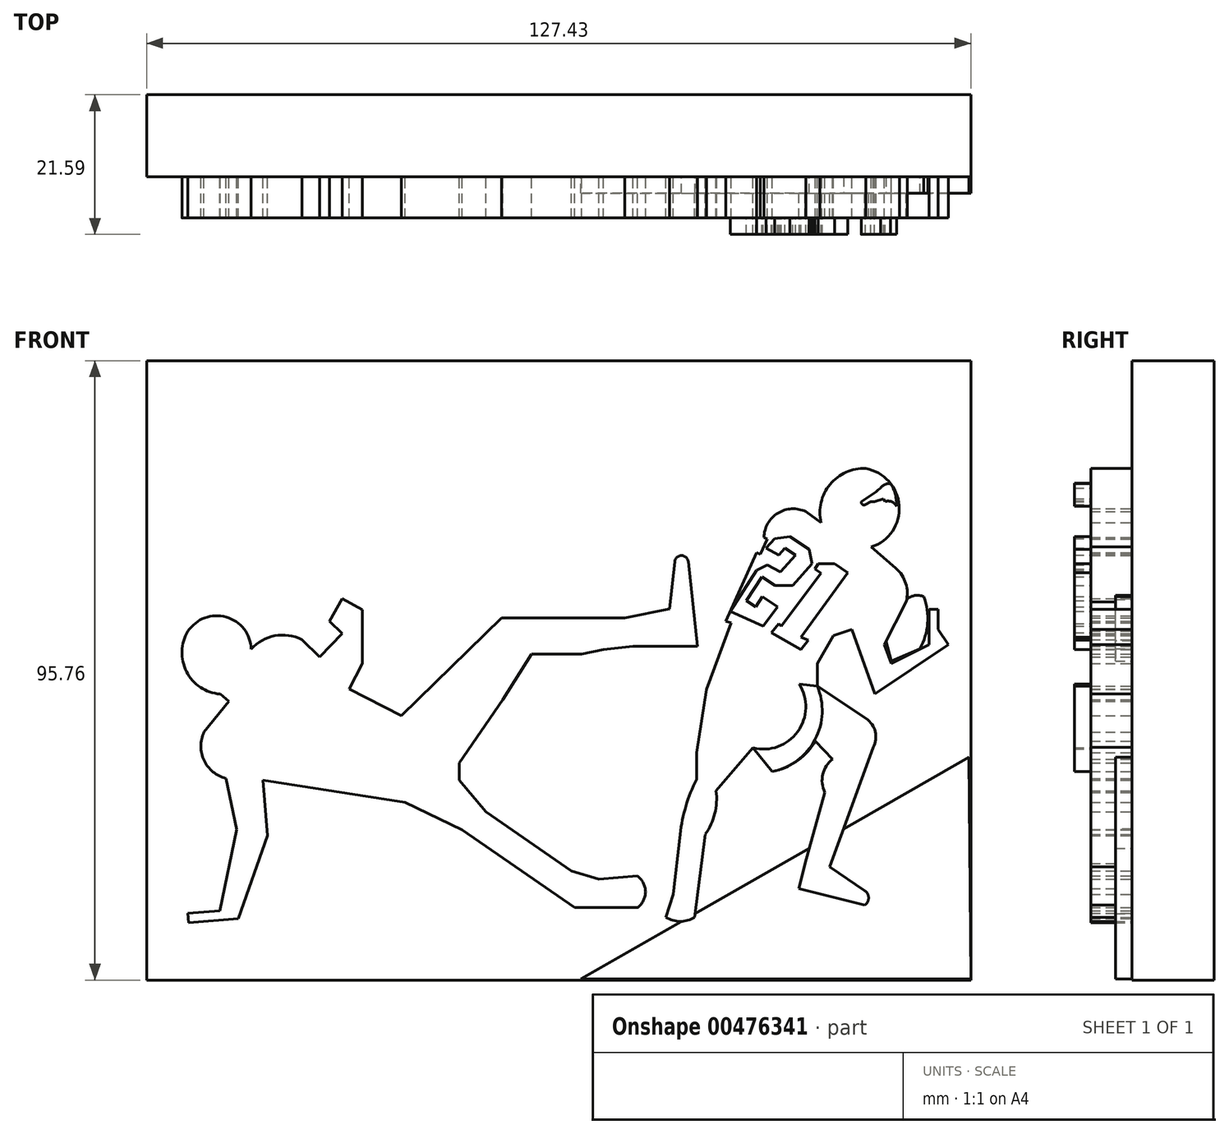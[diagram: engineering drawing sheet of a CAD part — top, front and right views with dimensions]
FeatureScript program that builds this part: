
annotation { "Feature Type Name" : "Feature", "Feature Type Description" : "" }
export const myFeature = defineFeature(function(context is Context, id is Id, definition is map)
    precondition{}
    {
        {
            var Q0;
            Q0=qCreatedBy(makeId("Front.planeOp"),FACE);
            var sketch = newSketch(context, id + "F0", { "sketchPlane" : qUnion([Q0])});
            skLineSegment(sketch, "E0.bottom", {"start": v(-88.04, 45.36) * mm, "end": v(39.4, 45.36) * mm});
            skLineSegment(sketch, "E0.top", {"start": v(-88.04, -50.4) * mm, "end": v(39.4, -50.4) * mm});
            skLineSegment(sketch, "E0.left", {"start": v(-88.04, 45.36) * mm, "end": v(-88.04, -50.4) * mm});
            skLineSegment(sketch, "E0.right", {"start": v(39.4, 45.36) * mm, "end": v(39.4, -50.4) * mm});
            skSolve(sketch);
        }
        {
            var Q0;
            Q0 = qSketchRegion(id + "F0", true);
            extrude(context, id + "F1", {"entities" : qUnion([Q0]), "depth" : 12.7 * mm});
        }
        {
            var Q0;
            Q0=makeQuery(id+"F1.opExtrude","CAP_FACE",FACE,{"disambiguationData":[OSD([sQuery(id+"F0.wireOp",EDGE,"E0.bottom"),sQuery(id+"F0.wireOp",EDGE,"E0.top"),sQuery(id+"F0.wireOp",EDGE,"E0.left"),sQuery(id+"F0.wireOp",EDGE,"E0.right")])],"isStart":false});
            var sketch = newSketch(context, id + "F2", { "sketchPlane" : qUnion([Q0])});
            skLineSegment(sketch, "E1", {"start": v(-70.07, -19.5) * mm, "end": v(-69.38, -28.1) * mm});
            skLineSegment(sketch, "E2", {"start": v(-69.38, -28.1) * mm, "end": v(-73.87, -40.93) * mm});
            skLineSegment(sketch, "E3", {"start": v(-73.87, -40.93) * mm, "end": v(-81.59, -41.55) * mm});
            skLineSegment(sketch, "E4", {"start": v(-81.59, -41.55) * mm, "end": v(-81.7, -40.06) * mm});
            skLineSegment(sketch, "E5", {"start": v(-81.7, -40.06) * mm, "end": v(-76.75, -39.66) * mm});
            skLineSegment(sketch, "E6", {"start": v(-76.75, -39.66) * mm, "end": v(-74.13, -27.12) * mm});
            skLineSegment(sketch, "E7", {"start": v(-74.13, -27.12) * mm, "end": v(-75.79, -19.23) * mm});
            skArc(sketch, "E8", {"start": v(-79.18, -12.07) * mm, "mid": v(-79.17, -16.45) * mm, "end": v(-75.79, -19.23) * mm});
            skLineSegment(sketch, "E9", {"start": v(-79.18, -12.07) * mm, "end": v(-75.33, -7.3) * mm});
            skLineSegment(sketch, "E10", {"start": v(-75.33, -7.3) * mm, "end": v(-76.7, -6.19) * mm});
            skArc(sketch, "E11", {"start": v(-81.65, 3.53) * mm, "mid": v(-81.89, -2.7) * mm, "end": v(-76.7, -6.19) * mm});
            skArc(sketch, "E12", {"start": v(-71.88, 0.74) * mm, "mid": v(-75.74, 5.72) * mm, "end": v(-81.65, 3.53) * mm});
            skArc(sketch, "E13", {"start": v(-64.06, 2.2) * mm, "mid": v(-68.22, 2.83) * mm, "end": v(-71.88, 0.74) * mm});
            skLineSegment(sketch, "E14", {"start": v(-64.06, 2.2) * mm, "end": v(-61.3, -0.45) * mm});
            skLineSegment(sketch, "E15", {"start": v(-61.3, -0.45) * mm, "end": v(-57.81, 3.16) * mm});
            skLineSegment(sketch, "E16", {"start": v(-57.81, 3.16) * mm, "end": v(-59.8, 5.08) * mm});
            skLineSegment(sketch, "E17", {"start": v(-59.8, 5.08) * mm, "end": v(-57.81, 8.58) * mm});
            skLineSegment(sketch, "E18", {"start": v(-57.81, 8.58) * mm, "end": v(-54.72, 6.83) * mm});
            skLineSegment(sketch, "E19", {"start": v(-54.72, 6.83) * mm, "end": v(-54.72, 3.16) * mm});
            skLineSegment(sketch, "E20", {"start": v(-54.72, 3.16) * mm, "end": v(-54.72, -1.48) * mm});
            skLineSegment(sketch, "E21", {"start": v(-54.72, -1.48) * mm, "end": v(-56.72, -5.4) * mm});
            skLineSegment(sketch, "E22", {"start": v(-56.72, -5.4) * mm, "end": v(-48.66, -9.52) * mm});
            skLineSegment(sketch, "E23", {"start": v(-48.66, -9.52) * mm, "end": v(-33.17, 5.59) * mm});
            skLineSegment(sketch, "E24", {"start": v(-33.17, 5.59) * mm, "end": v(-14.09, 5.59) * mm});
            skLineSegment(sketch, "E25", {"start": v(-14.09, 5.59) * mm, "end": v(-7.17, 6.98) * mm});
            skLineSegment(sketch, "E26", {"start": v(-7.17, 6.98) * mm, "end": v(-6.39, 14.29) * mm});
            skArc(sketch, "E27", {"start": v(-4.3, 14.29) * mm, "mid": v(-5.35, 15.22) * mm, "end": v(-6.39, 14.29) * mm});
            skLineSegment(sketch, "E28", {"start": v(-4.3, 14.29) * mm, "end": v(-2.9, 1.2) * mm});
            skLineSegment(sketch, "E29", {"start": v(-2.9, 1.2) * mm, "end": v(-12.85, 1.2) * mm});
            skLineSegment(sketch, "E30", {"start": v(-12.85, 1.2) * mm, "end": v(-17.44, 0.72) * mm});
            skLineSegment(sketch, "E31", {"start": v(-17.44, 0.72) * mm, "end": v(-20.76, 0) * mm});
            skLineSegment(sketch, "E32", {"start": v(-28.52, 0) * mm, "end": v(-20.76, 0) * mm});
            skLineSegment(sketch, "E33", {"start": v(-28.52, 0) * mm, "end": v(-32.95, -7.05) * mm});
            skLineSegment(sketch, "E34", {"start": v(-32.95, -7.05) * mm, "end": v(-39.73, -16.83) * mm});
            skLineSegment(sketch, "E35", {"start": v(-39.73, -16.83) * mm, "end": v(-39.73, -19.5) * mm});
            skLineSegment(sketch, "E36", {"start": v(-39.73, -19.5) * mm, "end": v(-35.57, -24.39) * mm});
            skLineSegment(sketch, "E37", {"start": v(-35.57, -24.39) * mm, "end": v(-22.34, -33.54) * mm});
            skLineSegment(sketch, "E38", {"start": v(-22.34, -33.54) * mm, "end": v(-18.15, -34.8) * mm});
            skLineSegment(sketch, "E39", {"start": v(-18.15, -34.8) * mm, "end": v(-12.17, -34.33) * mm});
            skArc(sketch, "E40", {"start": v(-12.17, -39.2) * mm, "mid": v(-10.9, -36.76) * mm, "end": v(-12.17, -34.33) * mm});
            skLineSegment(sketch, "E41", {"start": v(-12.17, -39.2) * mm, "end": v(-21.9, -39.2) * mm});
            skLineSegment(sketch, "E42", {"start": v(-21.9, -39.2) * mm, "end": v(-27.7, -35.18) * mm});
            skLineSegment(sketch, "E43", {"start": v(-27.7, -35.18) * mm, "end": v(-39.3, -27.16) * mm});
            skLineSegment(sketch, "E44", {"start": v(-39.3, -27.16) * mm, "end": v(-48.12, -22.92) * mm});
            skLineSegment(sketch, "E45", {"start": v(-48.12, -22.92) * mm, "end": v(-70.07, -19.5) * mm});
            skSolve(sketch);
        }
        {
            var Q0;
            Q0=makeQuery(id+"F2.imprint","IMPRINT",FACE,{"disambiguationData":[TD([[makeQuery(id+"F2.imprint","IMPRINT",EDGE,{"derivedFrom":sQuery(id+"F2.wireOp",EDGE,"E1")}),1.0]])]});
            var sketch = newSketch(context, id + "F3", { "sketchPlane" : qUnion([Q0])});
            skLineSegment(sketch, "E46", {"start": v(39.1, -15.97) * mm, "end": v(-20.94, -50.24) * mm});
            skLineSegment(sketch, "E47", {"start": v(39.1, -15.97) * mm, "end": v(39.39, -50.24) * mm});
            skLineSegment(sketch, "E48", {"start": v(-20.94, -50.24) * mm, "end": v(39.39, -50.24) * mm});
            skArc(sketch, "E49", {"start": v(32.1, 8.86) * mm, "mid": v(30.47, 9) * mm, "end": v(29.12, 8.06) * mm});
            skArc(sketch, "E50", {"start": v(31.51, 0.8) * mm, "mid": v(32.7, 4.77) * mm, "end": v(32.1, 8.86) * mm});
            skLineSegment(sketch, "E51", {"start": v(31.51, 0.8) * mm, "end": v(27.1, -1.08) * mm});
            skLineSegment(sketch, "E52", {"start": v(27.1, -1.08) * mm, "end": v(26.27, 2.07) * mm});
            skLineSegment(sketch, "E53", {"start": v(26.27, 2.07) * mm, "end": v(29.12, 8.06) * mm});
            skSolve(sketch);
        }
        {
            var Q0;
            Q0 = qSketchRegion(id + "F3", true);
            extrude(context, id + "F4", {"entities" : qUnion([Q0]), "depth" : 2.54 * mm});
        }
        {
            var Q0;
            Q0 = qSketchRegion(id + "F2", true);
            extrude(context, id + "F5", {"entities" : qUnion([Q0]), "depth" : 6.35 * mm});
        }
        {
            var Q0;
            Q0=makeQuery(id+"F2.imprint","IMPRINT",FACE,{"disambiguationData":[TD([[makeQuery(id+"F2.imprint","IMPRINT",EDGE,{"derivedFrom":sQuery(id+"F2.wireOp",EDGE,"E1")}),1.0]])]});
            var sketch = newSketch(context, id + "F6", { "sketchPlane" : qUnion([Q0])});
            skArc(sketch, "E54", {"start": v(-7.75, -40.7) * mm, "mid": v(-5.52, -41.33) * mm, "end": v(-3.3, -40.68) * mm});
            skLineSegment(sketch, "E55", {"start": v(-3.3, -40.68) * mm, "end": v(-1.67, -27.85) * mm});
            skLineSegment(sketch, "E56", {"start": v(-7.75, -40.7) * mm, "end": v(-6.61, -37.14) * mm});
            skLineSegment(sketch, "E57", {"start": v(-6.61, -37.14) * mm, "end": v(-5.55, -27.85) * mm});
            skArc(sketch, "E58", {"start": v(-3.03, -19.36) * mm, "mid": v(-4.66, -23.5) * mm, "end": v(-5.55, -27.85) * mm});
            skArc(sketch, "E59", {"start": v(-1.67, -27.85) * mm, "mid": v(-0.2, -24.67) * mm, "end": v(0, -21.17) * mm});
            skLineSegment(sketch, "E60", {"start": v(-3.03, -19.36) * mm, "end": v(-3.03, -15.26) * mm});
            skLineSegment(sketch, "E61", {"start": v(-3.03, -15.26) * mm, "end": v(-1.45, -5.45) * mm});
            skLineSegment(sketch, "E62", {"start": v(-1.45, -5.45) * mm, "end": v(2.32, 4.8) * mm});
            skLineSegment(sketch, "E63", {"start": v(2.32, 4.8) * mm, "end": v(1.52, 5.09) * mm});
            skLineSegment(sketch, "E64", {"start": v(1.52, 5.09) * mm, "end": v(6.25, 15.7) * mm});
            skLineSegment(sketch, "E65", {"start": v(6.25, 15.7) * mm, "end": v(6.84, 15.44) * mm});
            skLineSegment(sketch, "E66", {"start": v(6.84, 15.44) * mm, "end": v(7.9, 17.8) * mm});
            skLineSegment(sketch, "E67", {"start": v(7.9, 17.8) * mm, "end": v(7.4, 18.01) * mm});
            skArc(sketch, "E68", {"start": v(13.88, 22) * mm, "mid": v(9.55, 21.79) * mm, "end": v(7.4, 18.01) * mm});
            skLineSegment(sketch, "E69", {"start": v(13.88, 22) * mm, "end": v(16.25, 20.33) * mm});
            skArc(sketch, "E70", {"start": v(23.15, 28.68) * mm, "mid": v(17.61, 26.23) * mm, "end": v(16.25, 20.33) * mm});
            skArc(sketch, "E71", {"start": v(24, 16.54) * mm, "mid": v(28.32, 22.94) * mm, "end": v(23.15, 28.68) * mm});
            skLineSegment(sketch, "E72", {"start": v(24, 16.54) * mm, "end": v(27.78, 13.3) * mm});
            skArc(sketch, "E73", {"start": v(29.4, 8.08) * mm, "mid": v(29.34, 10.92) * mm, "end": v(27.78, 13.3) * mm});
            skLineSegment(sketch, "E74", {"start": v(29.4, 8.08) * mm, "end": v(25.99, 1.46) * mm});
            skLineSegment(sketch, "E75", {"start": v(25.99, 1.46) * mm, "end": v(27.1, -1.47) * mm});
            skLineSegment(sketch, "E76", {"start": v(27.1, -1.47) * mm, "end": v(32.96, 1.46) * mm});
            skLineSegment(sketch, "E77", {"start": v(32.96, 1.46) * mm, "end": v(32.96, 6.9) * mm});
            skLineSegment(sketch, "E78", {"start": v(32.96, 6.9) * mm, "end": v(34.35, 6.9) * mm});
            skLineSegment(sketch, "E79", {"start": v(34.35, 6.9) * mm, "end": v(34.35, 3.83) * mm});
            skLineSegment(sketch, "E80", {"start": v(34.35, 3.83) * mm, "end": v(35.04, 2.8) * mm});
            skLineSegment(sketch, "E81", {"start": v(35.04, 2.8) * mm, "end": v(35.94, 1.46) * mm});
            skLineSegment(sketch, "E82", {"start": v(35.94, 1.46) * mm, "end": v(24.53, -6.2) * mm});
            skLineSegment(sketch, "E83", {"start": v(24.53, -6.2) * mm, "end": v(20.97, 3.83) * mm});
            skLineSegment(sketch, "E84", {"start": v(20.97, 3.83) * mm, "end": v(18.16, 2.83) * mm});
            skLineSegment(sketch, "E85", {"start": v(18.16, 2.83) * mm, "end": v(15.64, -1.47) * mm});
            skLineSegment(sketch, "E86", {"start": v(15.64, -1.47) * mm, "end": v(15.64, -4.95) * mm});
            skLineSegment(sketch, "E87", {"start": v(15.64, -4.95) * mm, "end": v(23.22, -10) * mm});
            skArc(sketch, "E88", {"start": v(24.28, -14.45) * mm, "mid": v(24.62, -12.02) * mm, "end": v(23.22, -10) * mm});
            skLineSegment(sketch, "E89", {"start": v(24.28, -14.45) * mm, "end": v(17.57, -32.92) * mm});
            skLineSegment(sketch, "E90", {"start": v(17.57, -32.92) * mm, "end": v(22.98, -36.57) * mm});
            skArc(sketch, "E91", {"start": v(22.98, -38.82) * mm, "mid": v(23.58, -37.7) * mm, "end": v(22.98, -36.57) * mm});
            skLineSegment(sketch, "E92", {"start": v(22.98, -38.82) * mm, "end": v(12.79, -36.25) * mm});
            skLineSegment(sketch, "E93", {"start": v(12.79, -36.25) * mm, "end": v(13.77, -32.37) * mm});
            skLineSegment(sketch, "E94", {"start": v(13.77, -32.37) * mm, "end": v(16.8, -21.37) * mm});
            skArc(sketch, "E95", {"start": v(18.02, -16.24) * mm, "mid": v(16.5, -18.6) * mm, "end": v(16.8, -21.37) * mm});
            skLineSegment(sketch, "E96", {"start": v(0, -21.17) * mm, "end": v(5.7, -14.5) * mm});
            skLineSegment(sketch, "E97", {"start": v(5.7, -14.5) * mm, "end": v(8.68, -18.2) * mm});
            skArc(sketch, "E98", {"start": v(8.68, -18.2) * mm, "mid": v(12.51, -16.53) * mm, "end": v(15.35, -13.47) * mm});
            skLineSegment(sketch, "E99", {"start": v(15.35, -13.47) * mm, "end": v(18.02, -16.24) * mm});
            skSolve(sketch);
        }
        {
            var Q0;
            Q0 = qSketchRegion(id + "F6", true);
            extrude(context, id + "F7", {"entities" : qUnion([Q0]), "operationType" : NewBodyOperationType.ADD, "depth" : 6.35 * mm});
        }
        {
            var Q0;
            Q0=makeQuery(id+"F7.opExtrude","CAP_FACE",FACE,{"disambiguationData":[OSD([sQuery(id+"F6.wireOp",EDGE,"E54"),sQuery(id+"F6.wireOp",EDGE,"E55"),sQuery(id+"F6.wireOp",EDGE,"E56"),sQuery(id+"F6.wireOp",EDGE,"E57"),sQuery(id+"F6.wireOp",EDGE,"E58"),sQuery(id+"F6.wireOp",EDGE,"E59"),sQuery(id+"F6.wireOp",EDGE,"E60"),sQuery(id+"F6.wireOp",EDGE,"E61"),sQuery(id+"F6.wireOp",EDGE,"E62"),sQuery(id+"F6.wireOp",EDGE,"E63"),sQuery(id+"F6.wireOp",EDGE,"E64"),sQuery(id+"F6.wireOp",EDGE,"E65"),sQuery(id+"F6.wireOp",EDGE,"E66"),sQuery(id+"F6.wireOp",EDGE,"E67"),sQuery(id+"F6.wireOp",EDGE,"E68"),sQuery(id+"F6.wireOp",EDGE,"E69"),sQuery(id+"F6.wireOp",EDGE,"E70"),sQuery(id+"F6.wireOp",EDGE,"E71"),sQuery(id+"F6.wireOp",EDGE,"E72"),sQuery(id+"F6.wireOp",EDGE,"E73"),sQuery(id+"F6.wireOp",EDGE,"E74"),sQuery(id+"F6.wireOp",EDGE,"E75"),sQuery(id+"F6.wireOp",EDGE,"E76"),sQuery(id+"F6.wireOp",EDGE,"E77"),sQuery(id+"F6.wireOp",EDGE,"E78"),sQuery(id+"F6.wireOp",EDGE,"E79"),sQuery(id+"F6.wireOp",EDGE,"E80"),sQuery(id+"F6.wireOp",EDGE,"E81"),sQuery(id+"F6.wireOp",EDGE,"E82"),sQuery(id+"F6.wireOp",EDGE,"E83"),sQuery(id+"F6.wireOp",EDGE,"E84"),sQuery(id+"F6.wireOp",EDGE,"E85"),sQuery(id+"F6.wireOp",EDGE,"E86"),sQuery(id+"F6.wireOp",EDGE,"E87"),sQuery(id+"F6.wireOp",EDGE,"E88"),sQuery(id+"F6.wireOp",EDGE,"E89"),sQuery(id+"F6.wireOp",EDGE,"E90"),sQuery(id+"F6.wireOp",EDGE,"E91"),sQuery(id+"F6.wireOp",EDGE,"E92"),sQuery(id+"F6.wireOp",EDGE,"E93"),sQuery(id+"F6.wireOp",EDGE,"E94"),sQuery(id+"F6.wireOp",EDGE,"E95"),sQuery(id+"F6.wireOp",EDGE,"E96"),sQuery(id+"F6.wireOp",EDGE,"E97"),sQuery(id+"F6.wireOp",EDGE,"E98"),sQuery(id+"F6.wireOp",EDGE,"E99")])],"isStart":false});
            var sketch = newSketch(context, id + "F8", { "sketchPlane" : qUnion([Q0])});
            skLineSegment(sketch, "E100", {"start": v(12.86, -4.64) * mm, "end": v(15.64, -4.95) * mm});
            skLineSegment(sketch, "E101", {"start": v(5.7, -14.5) * mm, "end": v(8.68, -18.2) * mm});
            skArc(sketch, "E102", {"start": v(8.68, -18.2) * mm, "mid": v(15.3, -13.22) * mm, "end": v(15.64, -4.95) * mm});
            skArc(sketch, "E103", {"start": v(5.7, -14.5) * mm, "mid": v(12.63, -12) * mm, "end": v(12.86, -4.64) * mm});
            skLineSegment(sketch, "E104", {"start": v(9.5, 7.33) * mm, "end": v(7.3, 4.31) * mm});
            skLineSegment(sketch, "E105", {"start": v(7.3, 4.31) * mm, "end": v(2.19, 6.6) * mm});
            skLineSegment(sketch, "E106", {"start": v(2.19, 6.6) * mm, "end": v(6.25, 12.98) * mm});
            skLineSegment(sketch, "E107", {"start": v(6.25, 12.98) * mm, "end": v(7.9, 13.8) * mm});
            skLineSegment(sketch, "E108", {"start": v(7.9, 13.8) * mm, "end": v(9.94, 12.68) * mm});
            skLineSegment(sketch, "E109", {"start": v(9.94, 12.68) * mm, "end": v(12.28, 15.31) * mm});
            skLineSegment(sketch, "E110", {"start": v(12.28, 15.31) * mm, "end": v(10.65, 16.4) * mm});
            skLineSegment(sketch, "E111", {"start": v(10.65, 16.4) * mm, "end": v(9.7, 15.31) * mm});
            skLineSegment(sketch, "E112", {"start": v(9.7, 15.31) * mm, "end": v(7.75, 16.4) * mm});
            skLineSegment(sketch, "E113", {"start": v(7.75, 16.4) * mm, "end": v(9.04, 17.84) * mm});
            skLineSegment(sketch, "E114", {"start": v(9.04, 17.84) * mm, "end": v(11.43, 18.18) * mm});
            skLineSegment(sketch, "E115", {"start": v(11.43, 18.18) * mm, "end": v(14.42, 16.2) * mm});
            skLineSegment(sketch, "E116", {"start": v(14.42, 16.2) * mm, "end": v(14.8, 13.99) * mm});
            skLineSegment(sketch, "E117", {"start": v(14.8, 13.99) * mm, "end": v(11.83, 10.62) * mm});
            skLineSegment(sketch, "E118", {"start": v(11.83, 10.62) * mm, "end": v(9.15, 10.62) * mm});
            skLineSegment(sketch, "E119", {"start": v(9.15, 10.62) * mm, "end": v(7.12, 11.96) * mm});
            skLineSegment(sketch, "E120", {"start": v(7.12, 11.96) * mm, "end": v(4.68, 8.27) * mm});
            skLineSegment(sketch, "E121", {"start": v(4.68, 8.27) * mm, "end": v(6.13, 7.3) * mm});
            skLineSegment(sketch, "E122", {"start": v(6.13, 7.3) * mm, "end": v(7.18, 8.9) * mm});
            skLineSegment(sketch, "E123", {"start": v(7.18, 8.9) * mm, "end": v(9.5, 7.33) * mm});
            skLineSegment(sketch, "E124", {"start": v(16.23, 12.49) * mm, "end": v(15.25, 13.13) * mm});
            skLineSegment(sketch, "E125", {"start": v(15.25, 13.13) * mm, "end": v(15.81, 13.98) * mm});
            skLineSegment(sketch, "E126", {"start": v(15.81, 13.98) * mm, "end": v(18.33, 13.98) * mm});
            skLineSegment(sketch, "E127", {"start": v(18.33, 13.98) * mm, "end": v(20.39, 12.58) * mm});
            skLineSegment(sketch, "E128", {"start": v(20.39, 12.58) * mm, "end": v(13.15, 2.57) * mm});
            skLineSegment(sketch, "E129", {"start": v(13.15, 2.57) * mm, "end": v(14.28, 2.15) * mm});
            skLineSegment(sketch, "E130", {"start": v(14.28, 2.15) * mm, "end": v(13.1, 0.68) * mm});
            skLineSegment(sketch, "E131", {"start": v(13.1, 0.68) * mm, "end": v(8.53, 3.33) * mm});
            skLineSegment(sketch, "E132", {"start": v(8.53, 3.33) * mm, "end": v(9.7, 4.67) * mm});
            skLineSegment(sketch, "E133", {"start": v(9.7, 4.67) * mm, "end": v(10.1, 4.33) * mm});
            skLineSegment(sketch, "E134", {"start": v(10.1, 4.33) * mm, "end": v(16.23, 12.49) * mm});
            skArc(sketch, "E135", {"start": v(22.47, 23.57) * mm, "mid": v(24, 24.54) * mm, "end": v(25.41, 25.65) * mm});
            skArc(sketch, "E136", {"start": v(27, 26.37) * mm, "mid": v(26.11, 26.22) * mm, "end": v(25.41, 25.65) * mm});
            skArc(sketch, "E137", {"start": v(27.92, 22.82) * mm, "mid": v(27.71, 24.67) * mm, "end": v(27, 26.37) * mm});
            skArc(sketch, "E138", {"start": v(27.92, 22.82) * mm, "mid": v(27.17, 23.54) * mm, "end": v(26.13, 23.57) * mm});
            skLineSegment(sketch, "E139", {"start": v(26.13, 23.57) * mm, "end": v(25.86, 23.97) * mm});
            skLineSegment(sketch, "E140", {"start": v(25.86, 23.97) * mm, "end": v(24.48, 23.57) * mm});
            skLineSegment(sketch, "E141", {"start": v(24.48, 23.57) * mm, "end": v(23.89, 23.57) * mm});
            skLineSegment(sketch, "E142", {"start": v(23.89, 23.57) * mm, "end": v(23.11, 23.12) * mm});
            skArc(sketch, "E143", {"start": v(22.47, 23.57) * mm, "mid": v(22.63, 23.12) * mm, "end": v(23.11, 23.12) * mm});
            skSolve(sketch);
        }
        {
            var Q0;
            Q0 = qSketchRegion(id + "F8", true);
            extrude(context, id + "F9", {"entities" : qUnion([Q0]), "depth" : 2.54 * mm});
        }
    });
